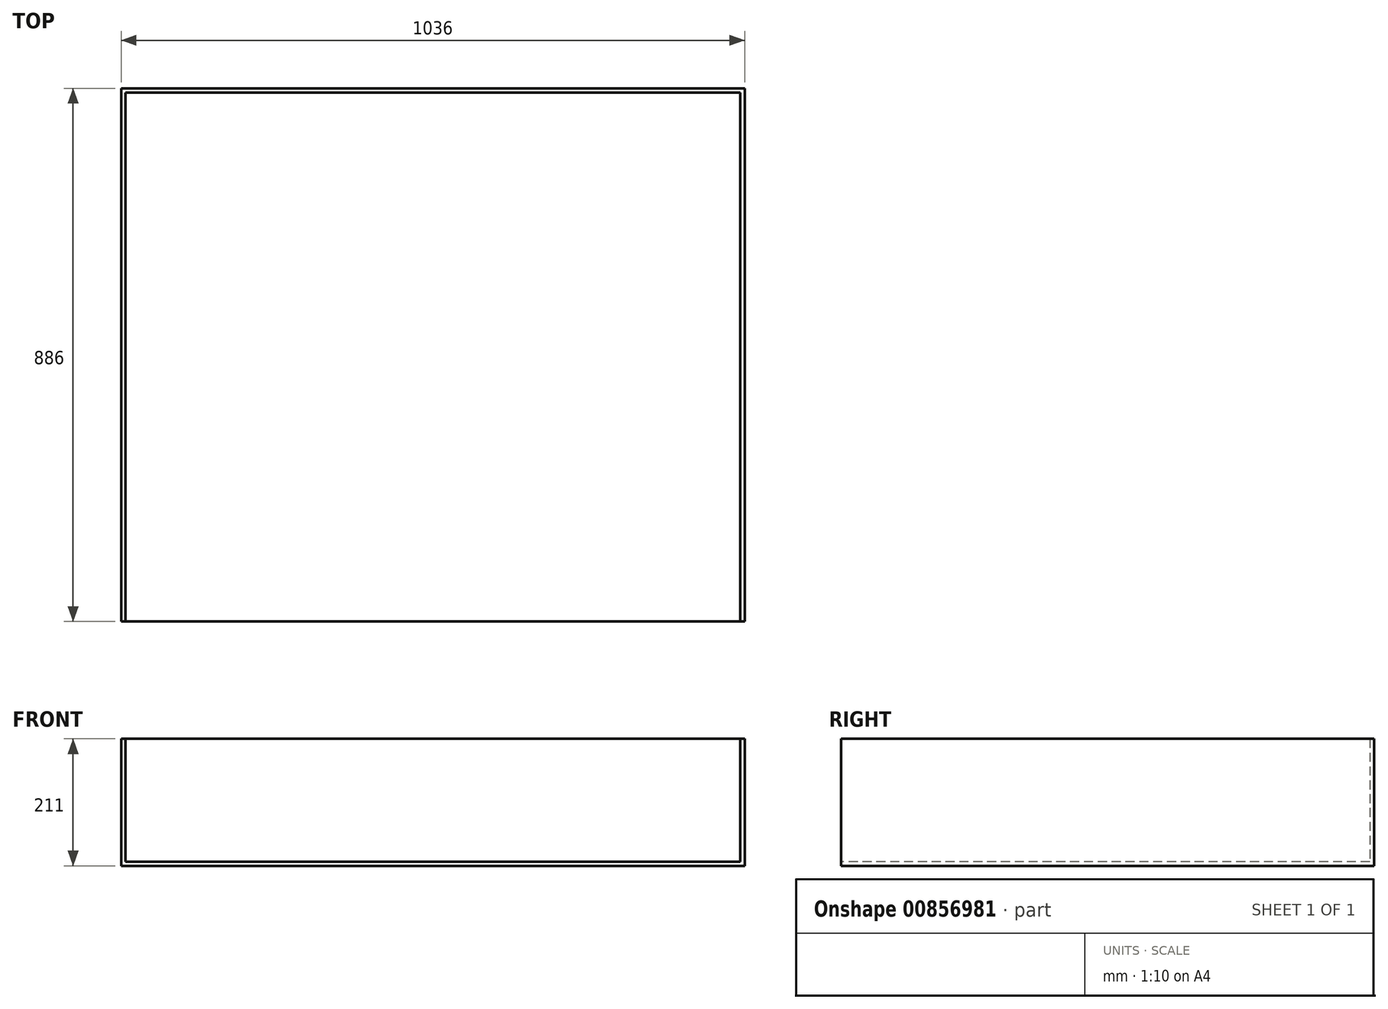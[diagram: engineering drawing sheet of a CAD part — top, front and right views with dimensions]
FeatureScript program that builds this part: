
annotation { "Feature Type Name" : "Feature", "Feature Type Description" : "" }
export const myFeature = defineFeature(function(context is Context, id is Id, definition is map)
    precondition{}
    {
        {
            var Q0;
            Q0=qCreatedBy(makeId("Front.planeOp"),FACE);
            var sketch = newSketch(context, id + "F0", { "sketchPlane" : qUnion([Q0])});
            skLineSegment(sketch, "E0.bottom", {"start": v(0, 0) * mm, "end": v(1036, 0) * mm});
            skLineSegment(sketch, "E0.top", {"start": v(0, -211) * mm, "end": v(1036, -211) * mm});
            skLineSegment(sketch, "E0.left", {"start": v(0, 0) * mm, "end": v(0, -211) * mm});
            skLineSegment(sketch, "E0.right", {"start": v(1036, 0) * mm, "end": v(1036, -211) * mm});
            skSolve(sketch);
        }
        {
            var Q0;
            Q0=makeQuery(id+"F0.imprint","IMPRINT",FACE,{"disambiguationData":[TD([[makeQuery(id+"F0.imprint","IMPRINT",EDGE,{"derivedFrom":sQuery(id+"F0.wireOp",EDGE,"E0.bottom")}),-1.0]])]});
            extrude(context, id + "F1", {"entities" : qUnion([Q0]), "oppositeDirection" : true, "depth" : 886 * mm, "offsetDistance" : 25 * mm});
        }
        {
            var Q0;
            Q0=makeQuery(id+"F1.opExtrude","SWEPT_FACE",FACE,{"disambiguationData":[OSD([sQuery(id+"F0.wireOp",EDGE,"E0.bottom")])]});
            var Q1;
            Q1=makeQuery(id+"F1.opExtrude","CAP_FACE",FACE,{"disambiguationData":[OSD([sQuery(id+"F0.wireOp",EDGE,"E0.bottom"),sQuery(id+"F0.wireOp",EDGE,"E0.top"),sQuery(id+"F0.wireOp",EDGE,"E0.left"),sQuery(id+"F0.wireOp",EDGE,"E0.right")])],"isStart":true});
            shell(context, id + "F2", {"entities" : qUnion([Q0, Q1]), "thickness" : 7 * mm});
        }
    });
